# Revit family: QF_BOURGEAT_4GN_bain_marie mobile_avec_etuve_cuve_separees
name_source: partatom
category: Equipement spécialisé
revit_build: Autodesk Revit 2015 (Build: 20140606_1530(x64)
units: mm (PartAtom-declared; Revit-internal decimal feet)

## types (2) — shared parameters
Charge max = 200.00 kg
Diamètre de Raccordement Evacuation = 27 mm
Fabricant = BOURGEAT
Fréquence = 50 Hz
Indice de protection = 33
Intensité nominale = 15 A
Longueur hors tout = 1665 mm  [stored 5.4626 ft]
Modèle = bain-marie mobiles OASIS
Nature isolant = 30mm laine de roche
Phase = 2
Profondeur hors tout = 701 mm  [stored 2.29987 ft]
Puissance électrique  = 3540 W
Tension = 230 V
URL catalogue = http://www.bourgeat.fr

## per-type parameters (varying)
| type | Couvercle | Hauteur hors tout | Poids net à vide | Spécification du Fabricant |
| GN4_bain_marie_mobile_avec_etuve_avec_couvercle | Oui | 960 mm  [stored 3.14961 ft] | 140.00 kg | 872414 |
| GN4_bain_marie_mobile_avec_etuve_sans_couvercle | Non | 900 mm  [stored 2.95276 ft] | 125.00 kg | 872214 |

note: [stored X ft] marks values corroborated as IEEE doubles in the binary element streams (Revit-internal decimal feet)
